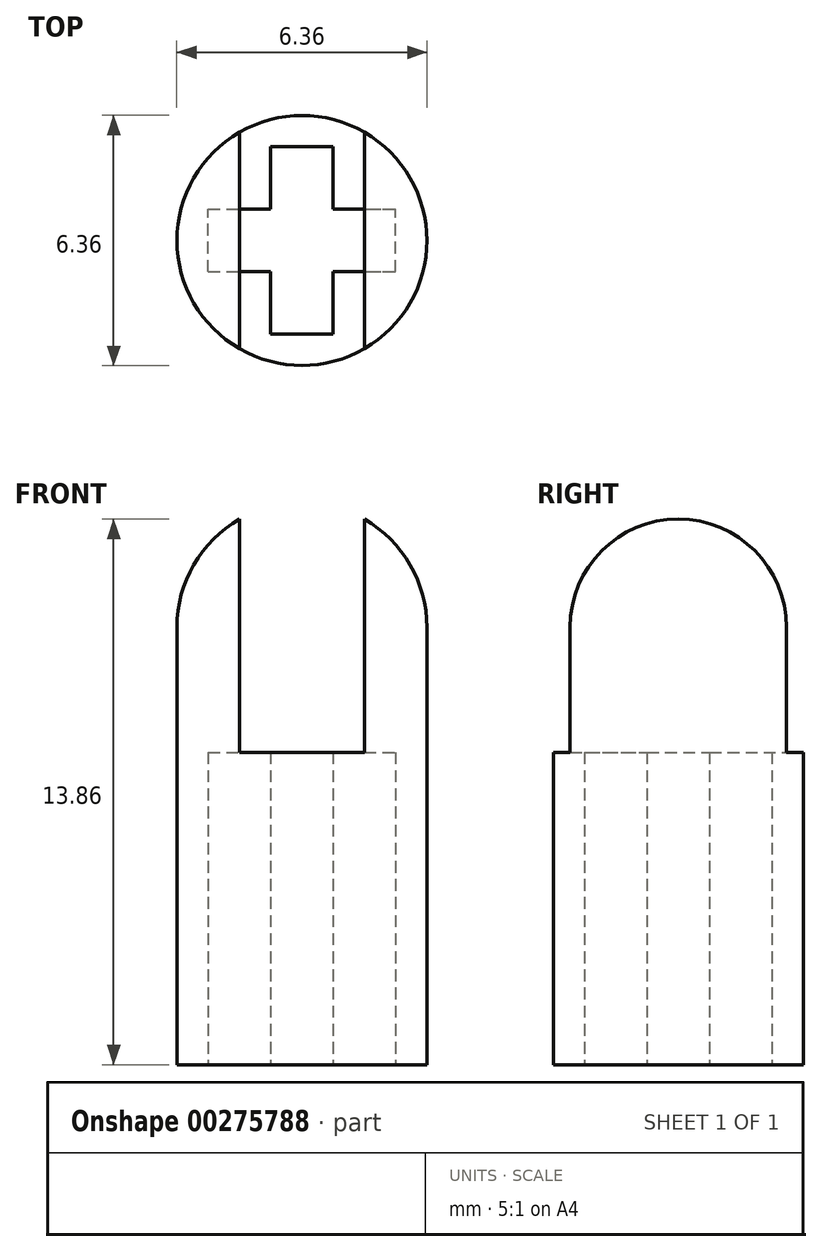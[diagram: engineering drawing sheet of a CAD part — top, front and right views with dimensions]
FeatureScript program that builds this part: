
annotation { "Feature Type Name" : "Feature", "Feature Type Description" : "" }
export const myFeature = defineFeature(function(context is Context, id is Id, definition is map)
    precondition{}
    {
        {
            var Q0;
            Q0=qCreatedBy(makeId("Top.planeOp"),FACE);
            var sketch = newSketch(context, id + "F0", { "sketchPlane" : qUnion([Q0])});
            skCircle(sketch, "E0", {"center": v(0, 0) * mm, "radius": 3.18 * mm});
            skSolve(sketch);
        }
        {
            var Q0;
            Q0=qSketchRegion(id+"F0",true);
            extrude(context, id + "F1", {"entities" : qUnion([Q0]), "depth" : 14.29 * mm});
        }
        {
            var Q0;
            Q0=makeQuery(id+"F1.opExtrude","CAP_EDGE",EDGE,{"disambiguationData":[OSD([sQuery(id+"F0.wireOp",EDGE,"E0")])],"isStart":false});
            fillet(context, id + "F2", {"entities" : qUnion([Q0]), "radius" : 3.17 * mm, "tangentPropagation" : true, "allowEdgeOverflow" : false});
        }
        {
            var Q0;
            Q0=qCreatedBy(makeId("Front.planeOp"),FACE);
            var sketch = newSketch(context, id + "F3", { "sketchPlane" : qUnion([Q0])});
            skLineSegment(sketch, "E1", {"start": v(0, 0) * mm, "end": v(0, 7.94) * mm});
            skLineSegment(sketch, "E2", {"start": v(0, 7.94) * mm, "end": v(-1.59, 7.94) * mm});
            skLineSegment(sketch, "E3.MirrorCS", {"start": v(0, 7.94) * mm, "end": v(1.59, 7.94) * mm});
            skLineSegment(sketch, "E4.bottom", {"start": v(-1.59, 7.94) * mm, "end": v(1.59, 7.94) * mm});
            skLineSegment(sketch, "E4.top", {"start": v(-1.59, 14.9) * mm, "end": v(1.59, 14.9) * mm});
            skLineSegment(sketch, "E4.left", {"start": v(-1.59, 7.94) * mm, "end": v(-1.59, 14.9) * mm});
            skLineSegment(sketch, "E4.right", {"start": v(1.59, 7.94) * mm, "end": v(1.59, 14.9) * mm});
            skSolve(sketch);
        }
        {
            var Q0;
            Q0=qSketchRegion(id+"F3",true);
            extrude(context, id + "F4", {"entities" : qUnion([Q0]), "operationType" : NewBodyOperationType.REMOVE, "endBound" : BoundingType.SYMMETRIC, "depth" : 25.4 * mm});
        }
        {
            var Q0;
            Q0=makeQuery(id+"F1.opExtrude","CAP_FACE",FACE,{"disambiguationData":[OSD([sQuery(id+"F0.wireOp",EDGE,"E0")])],"isStart":true});
            var sketch = newSketch(context, id + "F5", { "sketchPlane" : qUnion([Q0])});
            skLineSegment(sketch, "E5.bottom", {"start": v(-2.38, 0.8) * mm, "end": v(2.38, 0.8) * mm});
            skLineSegment(sketch, "E5.top", {"start": v(-2.38, -0.8) * mm, "end": v(2.38, -0.8) * mm});
            skLineSegment(sketch, "E5.left", {"start": v(-2.38, 0.8) * mm, "end": v(-2.38, -0.8) * mm});
            skLineSegment(sketch, "E5.right", {"start": v(2.38, 0.8) * mm, "end": v(2.38, -0.8) * mm});
            skPoint(sketch, "E5.middle", {"position": v(0, 0) * mm});
            skLineSegment(sketch, "E6.bottom", {"start": v(-0.8, 2.38) * mm, "end": v(0.8, 2.38) * mm});
            skLineSegment(sketch, "E6.top", {"start": v(-0.8, -2.38) * mm, "end": v(0.8, -2.38) * mm});
            skLineSegment(sketch, "E6.left", {"start": v(-0.8, 2.38) * mm, "end": v(-0.8, -2.38) * mm});
            skLineSegment(sketch, "E6.right", {"start": v(0.8, 2.38) * mm, "end": v(0.8, -2.38) * mm});
            skSolve(sketch);
        }
        {
            var Q0;
            Q0=qSketchRegion(id+"F5",true);
            extrude(context, id + "F6", {"entities" : qUnion([Q0]), "operationType" : NewBodyOperationType.REMOVE, "oppositeDirection" : true, "depth" : 7.94 * mm});
        }
    });
